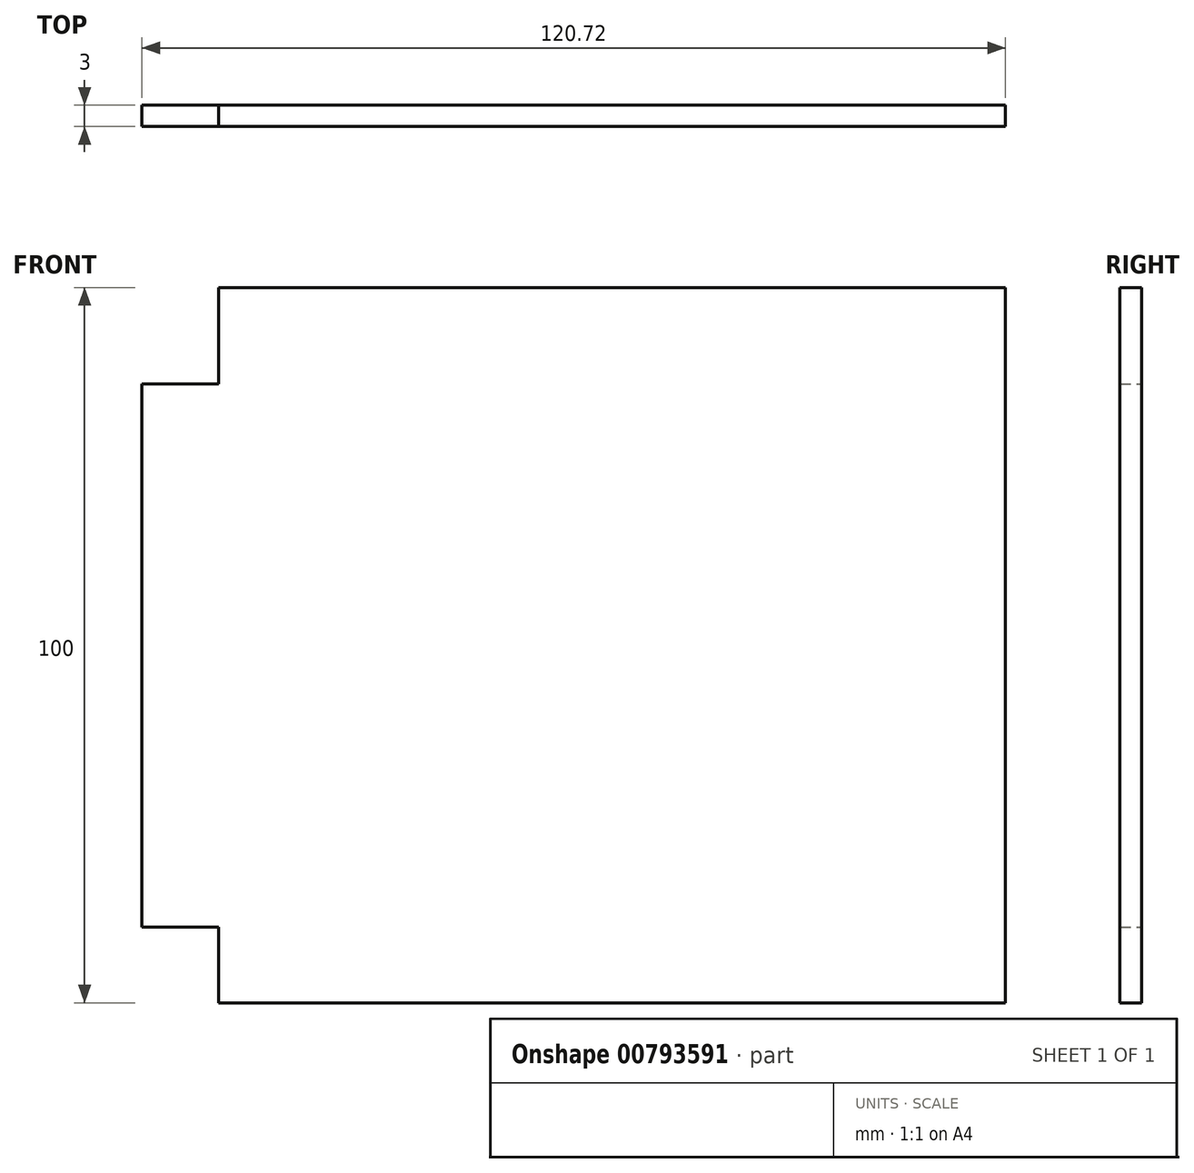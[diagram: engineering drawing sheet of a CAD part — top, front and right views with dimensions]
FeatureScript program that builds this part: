
annotation { "Feature Type Name" : "Feature", "Feature Type Description" : "" }
export const myFeature = defineFeature(function(context is Context, id is Id, definition is map)
    precondition{}
    {
        {
            var Q0;
            Q0=qCreatedBy(makeId("Front.planeOp"),FACE);
            var sketch = newSketch(context, id + "F0", { "sketchPlane" : qUnion([Q0])});
            skLineSegment(sketch, "E0.bottom", {"start": v(-54, 62.64) * mm, "end": v(56, 62.64) * mm});
            skLineSegment(sketch, "E0.top", {"start": v(-54, -37.36) * mm, "end": v(56, -37.36) * mm});
            skLineSegment(sketch, "E0.left", {"start": v(-54, 62.64) * mm, "end": v(-54, -37.36) * mm});
            skLineSegment(sketch, "E0.right", {"start": v(56, 62.64) * mm, "end": v(56, -37.36) * mm});
            skLineSegment(sketch, "E1", {"start": v(-54, 62.64) * mm, "end": v(-54, 49.15) * mm});
            skLineSegment(sketch, "E2", {"start": v(-54, 49.15) * mm, "end": v(-64.73, 49.15) * mm});
            skLineSegment(sketch, "E3", {"start": v(-64.73, 49.15) * mm, "end": v(-64.73, -26.77) * mm});
            skLineSegment(sketch, "E4", {"start": v(-64.73, -26.77) * mm, "end": v(-54, -26.77) * mm});
            skSolve(sketch);
        }
        {
            var Q0;
            Q0 = qSketchRegion(id + "F0", true);
            extrude(context, id + "F1", {"entities" : qUnion([Q0]), "depth" : 3 * mm, "offsetDistance" : 25 * mm});
        }
    });
